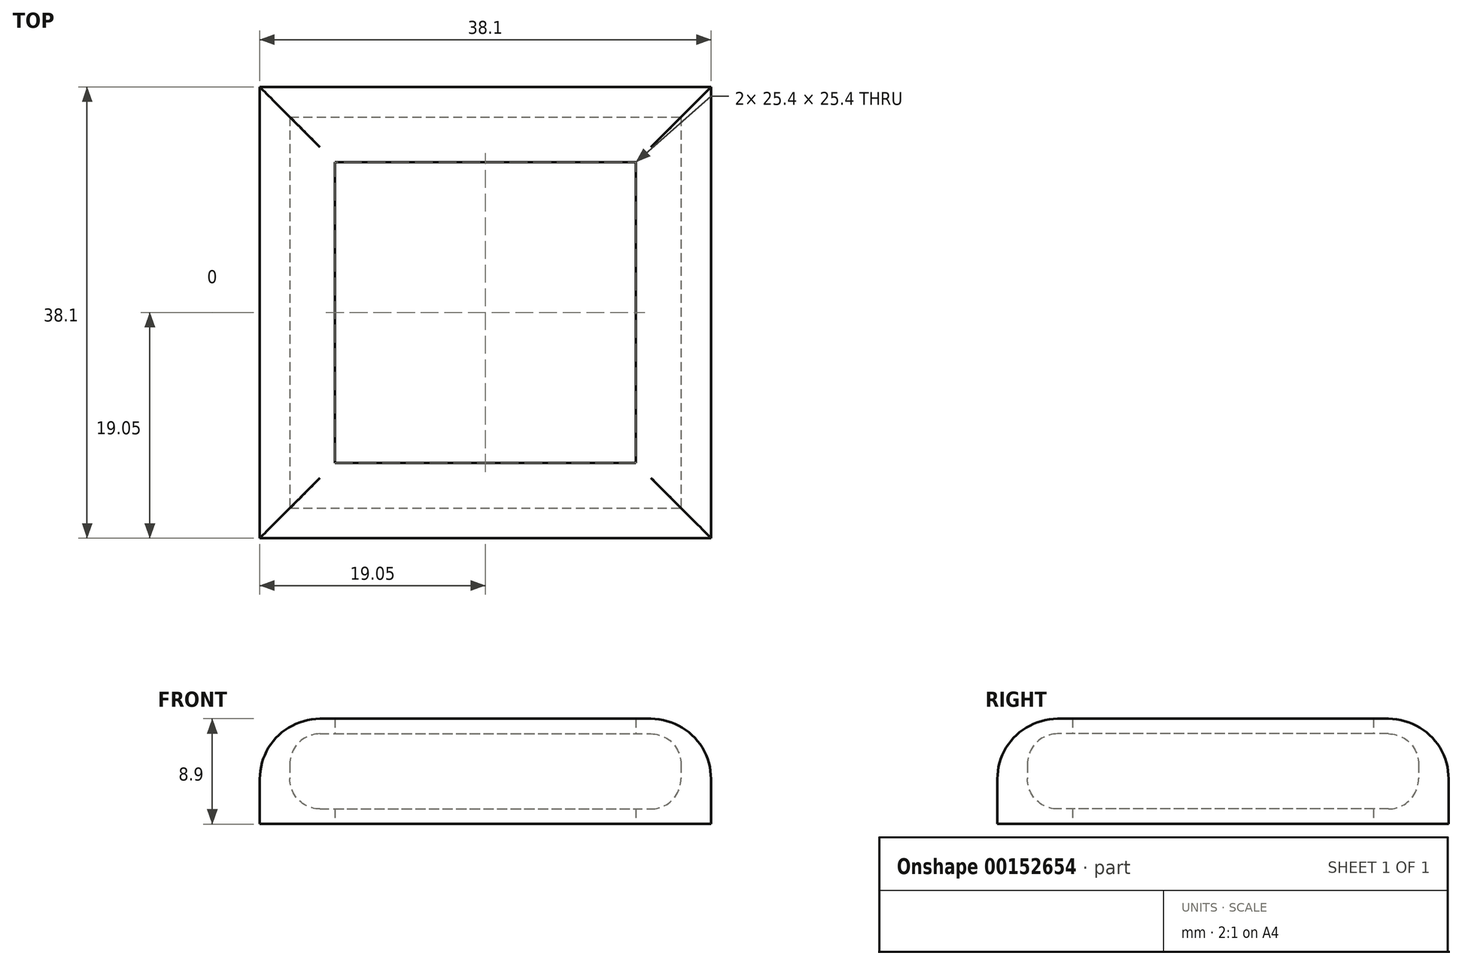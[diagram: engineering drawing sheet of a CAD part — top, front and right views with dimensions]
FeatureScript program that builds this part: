
annotation { "Feature Type Name" : "Feature", "Feature Type Description" : "" }
export const myFeature = defineFeature(function(context is Context, id is Id, definition is map)
    precondition{}
    {
        {
            var Q0;
            Q0=qCreatedBy(makeId("Top.planeOp"),FACE);
            var sketch = newSketch(context, id + "F0", { "sketchPlane" : qUnion([Q0])});
            skLineSegment(sketch, "E0.bottom", {"start": v(-19.05, 19.05) * mm, "end": v(19.05, 19.05) * mm});
            skLineSegment(sketch, "E0.top", {"start": v(-19.05, -19.05) * mm, "end": v(19.05, -19.05) * mm});
            skLineSegment(sketch, "E0.left", {"start": v(-19.05, 19.05) * mm, "end": v(-19.05, -19.05) * mm});
            skLineSegment(sketch, "E0.right", {"start": v(19.05, 19.05) * mm, "end": v(19.05, -19.05) * mm});
            skPoint(sketch, "E1", {"position": v(0, 19.05) * mm});
            skLineSegment(sketch, "E2.bottom", {"start": v(-12.7, 12.7) * mm, "end": v(12.7, 12.7) * mm});
            skLineSegment(sketch, "E2.top", {"start": v(-12.7, -12.7) * mm, "end": v(12.7, -12.7) * mm});
            skLineSegment(sketch, "E2.left", {"start": v(-12.7, 12.7) * mm, "end": v(-12.7, -12.7) * mm});
            skLineSegment(sketch, "E2.right", {"start": v(12.7, 12.7) * mm, "end": v(12.7, -12.7) * mm});
            skPoint(sketch, "E2.middle", {"position": v(0, 0) * mm});
            skLineSegment(sketch, "E3", {"start": v(-19.05, 5.73) * mm, "end": v(-12.7, 5.73) * mm, "construction": true});
            skLineSegment(sketch, "E4", {"start": v(-3.58, -12.7) * mm, "end": v(-3.58, -19.05) * mm, "construction": true});
            skLineSegment(sketch, "E5", {"start": v(-8.63, 19.05) * mm, "end": v(-8.63, 12.7) * mm, "construction": true});
            skLineSegment(sketch, "E6", {"start": v(19.05, 5.8) * mm, "end": v(12.7, 5.8) * mm, "construction": true});
            skLineSegment(sketch, "E7.bottom", {"start": v(-16.51, 16.51) * mm, "end": v(16.51, 16.51) * mm});
            skLineSegment(sketch, "E7.top", {"start": v(-16.51, -16.51) * mm, "end": v(16.51, -16.51) * mm});
            skLineSegment(sketch, "E7.left", {"start": v(-16.51, 16.51) * mm, "end": v(-16.51, -16.51) * mm});
            skLineSegment(sketch, "E7.right", {"start": v(16.51, 16.51) * mm, "end": v(16.51, -16.51) * mm});
            skSolve(sketch);
        }
        {
            var Q0;
            Q0=makeQuery(id+"F0.imprint","IMPRINT",FACE,{"disambiguationData":[TD([[makeQuery(id+"F0.imprint","IMPRINT",EDGE,{"derivedFrom":sQuery(id+"F0.wireOp",EDGE,"E0.bottom")}),-1.0]])]});
            var Q1;
            Q1=makeQuery(id+"F0.imprint","IMPRINT",FACE,{"disambiguationData":[TD([[makeQuery(id+"F0.imprint","IMPRINT",EDGE,{"derivedFrom":sQuery(id+"F0.wireOp",EDGE,"E2.bottom")}),1.0]])]});
            extrude(context, id + "F1", {"entities" : qUnion([Q0, Q1]), "depth" : 4.44 * mm, "hasSecondDirection" : true, "secondDirectionOppositeDirection" : true, "secondDirectionDepth" : 4.44 * mm});
        }
        {
            var Q0;
            Q0=makeQuery(id+"F0.imprint","IMPRINT",FACE,{"disambiguationData":[TD([[makeQuery(id+"F0.imprint","IMPRINT",EDGE,{"derivedFrom":sQuery(id+"F0.wireOp",EDGE,"E2.bottom")}),1.0]])]});
            extrude(context, id + "F2", {"entities" : qUnion([Q0]), "operationType" : NewBodyOperationType.REMOVE, "depth" : 3.17 * mm, "hasSecondDirection" : true, "secondDirectionOppositeDirection" : true, "secondDirectionDepth" : 3.17 * mm});
        }
        {
            var Q0;
            Q0=makeQuery(id+"F2.boolean.opBoolean","COPY",EDGE,{"derivedFrom":makeQuery(id+"F2.opExtrude","CAP_EDGE",EDGE,{"disambiguationData":[OSD([sQuery(id+"F0.wireOp",EDGE,"E7.left")])],"isStart":true})});
            var Q1;
            Q1=makeQuery(id+"F2.boolean.opBoolean","COPY",EDGE,{"derivedFrom":makeQuery(id+"F2.opExtrude","CAP_EDGE",EDGE,{"disambiguationData":[OSD([sQuery(id+"F0.wireOp",EDGE,"E7.bottom")])],"isStart":true})});
            var Q2;
            Q2=makeQuery(id+"F2.boolean.opBoolean","COPY",EDGE,{"derivedFrom":makeQuery(id+"F2.opExtrude","CAP_EDGE",EDGE,{"disambiguationData":[OSD([sQuery(id+"F0.wireOp",EDGE,"E7.right")])],"isStart":true})});
            var Q3;
            Q3=makeQuery(id+"F2.boolean.opBoolean","COPY",EDGE,{"derivedFrom":makeQuery(id+"F2.opExtrude","CAP_EDGE",EDGE,{"disambiguationData":[OSD([sQuery(id+"F0.wireOp",EDGE,"E7.top")])],"isStart":true})});
            fillet(context, id + "F3", {"entities" : qUnion([Q0, Q1, Q2, Q3]), "radius" : 2.54 * mm, "tangentPropagation" : true, "allowEdgeOverflow" : false});
        }
        {
            var Q0;
            Q0=makeQuery(id+"F2.boolean.opBoolean","COPY",EDGE,{"derivedFrom":makeQuery(id+"F2.opExtrude","CAP_EDGE",EDGE,{"disambiguationData":[OSD([sQuery(id+"F0.wireOp",EDGE,"E7.bottom")])],"isStart":false})});
            var Q1;
            Q1=makeQuery(id+"F2.boolean.opBoolean","COPY",EDGE,{"derivedFrom":makeQuery(id+"F2.opExtrude","CAP_EDGE",EDGE,{"disambiguationData":[OSD([sQuery(id+"F0.wireOp",EDGE,"E7.right")])],"isStart":false})});
            var Q2;
            Q2=makeQuery(id+"F2.boolean.opBoolean","COPY",EDGE,{"derivedFrom":makeQuery(id+"F2.opExtrude","CAP_EDGE",EDGE,{"disambiguationData":[OSD([sQuery(id+"F0.wireOp",EDGE,"E7.top")])],"isStart":false})});
            var Q3;
            Q3=makeQuery(id+"F2.boolean.opBoolean","COPY",EDGE,{"derivedFrom":makeQuery(id+"F2.opExtrude","CAP_EDGE",EDGE,{"disambiguationData":[OSD([sQuery(id+"F0.wireOp",EDGE,"E7.left")])],"isStart":false})});
            fillet(context, id + "F4", {"entities" : qUnion([Q0, Q1, Q2, Q3]), "radius" : 2.54 * mm, "tangentPropagation" : true, "allowEdgeOverflow" : false});
        }
        {
            var Q0;
            Q0=makeQuery(id+"F1.opExtrude","CAP_EDGE",EDGE,{"disambiguationData":[OSD([sQuery(id+"F0.wireOp",EDGE,"E0.right")])],"isStart":false});
            var Q1;
            Q1=makeQuery(id+"F1.opExtrude","CAP_EDGE",EDGE,{"disambiguationData":[OSD([sQuery(id+"F0.wireOp",EDGE,"E0.bottom")])],"isStart":false});
            var Q2;
            Q2=makeQuery(id+"F1.opExtrude","CAP_EDGE",EDGE,{"disambiguationData":[OSD([sQuery(id+"F0.wireOp",EDGE,"E0.left")])],"isStart":false});
            var Q3;
            Q3=makeQuery(id+"F1.opExtrude","CAP_EDGE",EDGE,{"disambiguationData":[OSD([sQuery(id+"F0.wireOp",EDGE,"E0.top")])],"isStart":false});
            fillet(context, id + "F5", {"entities" : qUnion([Q0, Q1, Q2, Q3]), "radius" : 5.08 * mm, "tangentPropagation" : true, "allowEdgeOverflow" : false});
        }
    });
